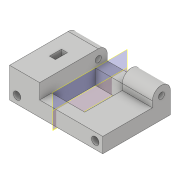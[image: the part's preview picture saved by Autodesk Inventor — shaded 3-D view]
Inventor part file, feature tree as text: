
AUTODESK INVENTOR PART (.ipt)
format: ipt  version: 2019 (Build 230136000, 136)  size: 188,416 bytes
history: native  units: mm
features: extrude x6, sketch x6, projected_geometry x5, plane x2, mirror x2
ambient origin geometry x8: Origin, YZ Plane, XZ Plane, XY Plane, X Axis, Y Axis, Z Axis, Center Point
bodies: Solid1 (feature_tree)
feature tree (21):
  extrude  "Extrusion1"  Depth=31.0mm
  extrude  "Extrusion2"  Depth=5.0mm
  plane  "Work Plane1"
  mirror  "Mirror1"
  extrude  "Extrusion3"  Depth=5.0mm TaperAngle=0.0deg
  extrude  "Extrusion4"  Depth=4.0mm
  plane  "Work Plane2"
  mirror  "Mirror2"
  extrude  "Extrusion6"  Depth=5.0mm TaperAngle=0.0deg
  extrude  "Extrusion7"  Depth=2.0mm
  sketch  "Sketch1"  dims[d0=22.5mm d1=31.0mm]
  sketch  "Sketch2"  dims[d2=5.0mm d3=0.0mm d4=2.5mm]
  projected_geometry  "Projected Loop1"
  sketch  "Sketch3"  dims[d5=2.5mm d6=5.0mm d7=0.0mm]
  projected_geometry  "Projected Loop2"
  sketch  "Sketch4"  dims[d8=4.0mm d9=4.0mm]
  projected_geometry  "Projected Loop3"
  sketch  "Sketch6"  dims[d11=11.0mm d12=5.0mm d13=0.0mm]
  projected_geometry  "Projected Loop5"
  sketch  "Sketch7"  dims[d16=10.0mm d17=0.0mm d21=2.0mm d22=3.0mm d23=2.0mm d26=12.0mm d27=0.0mm d28=2.0mm d29=4.0mm d30=5.0mm d31=0.0mm]
  projected_geometry  "Projected Loop6"
